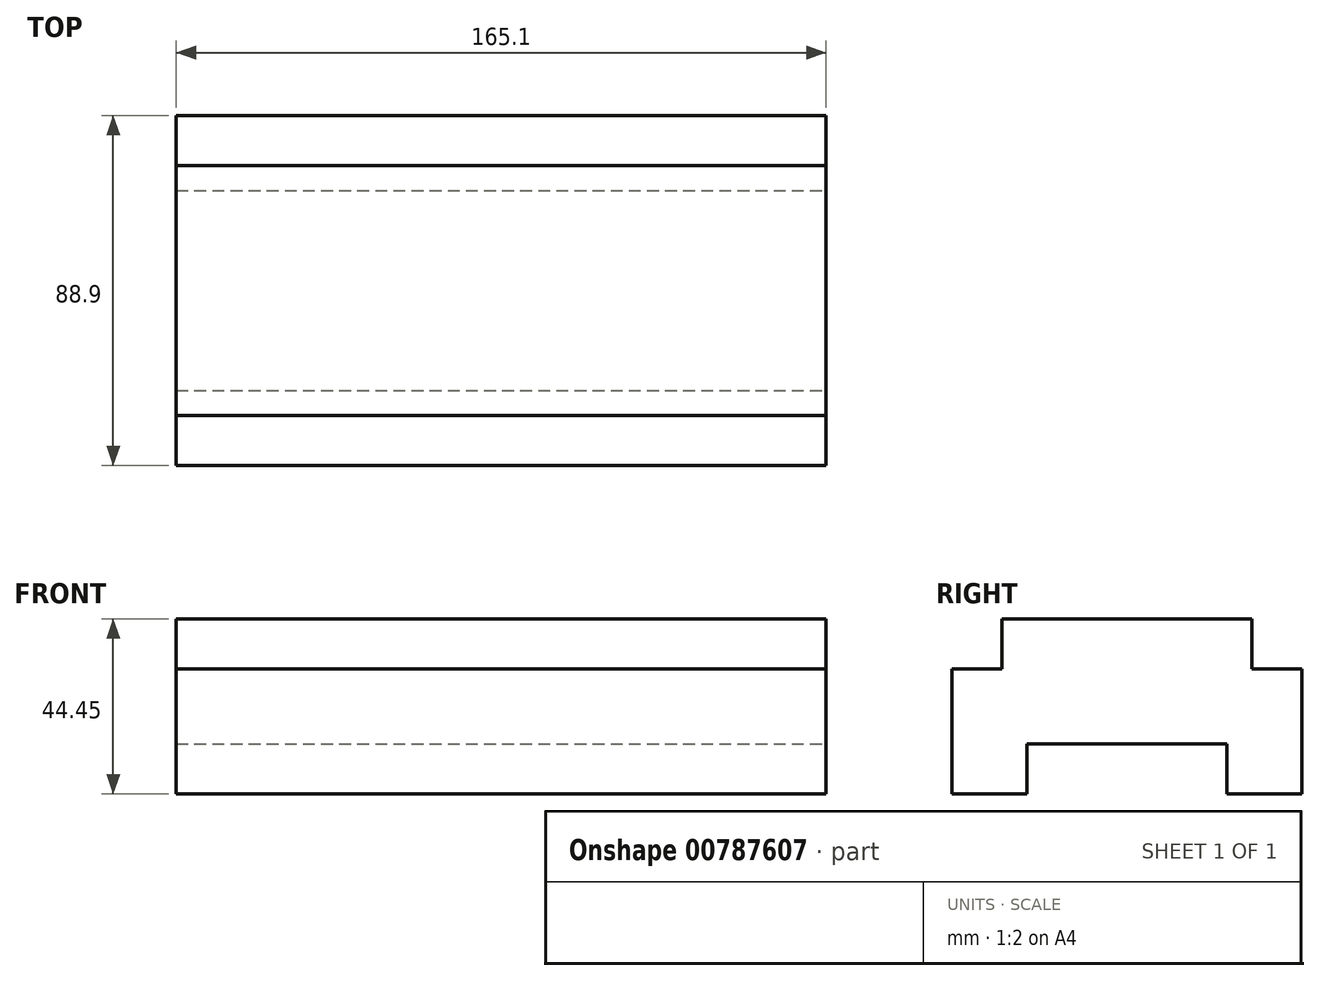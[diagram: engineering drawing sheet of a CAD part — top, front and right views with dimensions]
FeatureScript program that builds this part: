
annotation { "Feature Type Name" : "Feature", "Feature Type Description" : "" }
export const myFeature = defineFeature(function(context is Context, id is Id, definition is map)
    precondition{}
    {
        {
            var Q0;
            Q0=qCreatedBy(makeId("Front.planeOp"),FACE);
            var sketch = newSketch(context, id + "F0", { "sketchPlane" : qUnion([Q0])});
            skLineSegment(sketch, "E0", {"start": v(0, 0) * mm, "end": v(165.1, 0) * mm});
            skLineSegment(sketch, "E1", {"start": v(0, 0) * mm, "end": v(0, 44.45) * mm});
            skLineSegment(sketch, "E2", {"start": v(165.1, 0) * mm, "end": v(165.1, 44.45) * mm});
            skLineSegment(sketch, "E3", {"start": v(0, 44.45) * mm, "end": v(165.1, 44.45) * mm});
            skSolve(sketch);
        }
        {
            var Q0;
            Q0=makeQuery(id+"F0.imprint","IMPRINT",FACE,{"disambiguationData":[TD([[makeQuery(id+"F0.imprint","IMPRINT",EDGE,{"derivedFrom":sQuery(id+"F0.wireOp",EDGE,"E0")}),1.0]])]});
            extrude(context, id + "F1", {"entities" : qUnion([Q0]), "depth" : 88.9 * mm, "offsetDistance" : 25.4 * mm});
        }
        {
            var Q0;
            Q0=makeQuery(id+"F1.opExtrude","SWEPT_FACE",FACE,{"disambiguationData":[OSD([sQuery(id+"F0.wireOp",EDGE,"E2")])]});
            var sketch = newSketch(context, id + "F2", { "sketchPlane" : qUnion([Q0])});
            skLineSegment(sketch, "E4", {"start": v(-69.85, 0) * mm, "end": v(-69.85, 12.7) * mm});
            skLineSegment(sketch, "E5", {"start": v(-69.85, 12.7) * mm, "end": v(-19.05, 12.7) * mm});
            skLineSegment(sketch, "E6", {"start": v(-19.05, 12.7) * mm, "end": v(-19.05, 0) * mm});
            skSolve(sketch);
        }
        {
            var Q0;
            {var subQ0=sQuery(id+"F2.wireOp",EDGE,"E4");Q0=makeQuery(id+"F2.imprint","IMPRINT",FACE,{"disambiguationData":[TD([[makeQuery(id+"F2.imprint","IMPRINT",EDGE,{"derivedFrom":subQ0}),-1.0]])]});}
            extrude(context, id + "F3", {"entities" : qUnion([Q0]), "operationType" : NewBodyOperationType.REMOVE, "oppositeDirection" : true, "depth" : 165.1 * mm, "offsetDistance" : 25.4 * mm});
        }
        {
            var Q0;
            Q0=makeQuery(id+"F1.opExtrude","SWEPT_FACE",FACE,{"disambiguationData":[OSD([sQuery(id+"F0.wireOp",EDGE,"E2")])]});
            var sketch = newSketch(context, id + "F4", { "sketchPlane" : qUnion([Q0])});
            skLineSegment(sketch, "E7", {"start": v(-88.9, 31.75) * mm, "end": v(-76.2, 31.75) * mm});
            skLineSegment(sketch, "E8", {"start": v(-76.2, 31.75) * mm, "end": v(-76.2, 44.45) * mm});
            skLineSegment(sketch, "E9", {"start": v(0, 31.75) * mm, "end": v(-12.7, 31.75) * mm});
            skLineSegment(sketch, "E10", {"start": v(-12.7, 31.75) * mm, "end": v(-12.7, 44.45) * mm});
            skSolve(sketch);
        }
        {
            var Q0;
            {var subQ0=sQuery(id+"F4.wireOp",EDGE,"E7");Q0=makeQuery(id+"F4.imprint","IMPRINT",FACE,{"disambiguationData":[TD([[makeQuery(id+"F4.imprint","IMPRINT",EDGE,{"derivedFrom":subQ0}),1.0]])]});}
            var Q1;
            {var subQ0=sQuery(id+"F4.wireOp",EDGE,"E9");Q1=makeQuery(id+"F4.imprint","IMPRINT",FACE,{"disambiguationData":[TD([[makeQuery(id+"F4.imprint","IMPRINT",EDGE,{"derivedFrom":subQ0}),-1.0]])]});}
            extrude(context, id + "F5", {"entities" : qUnion([Q0, Q1]), "operationType" : NewBodyOperationType.REMOVE, "oppositeDirection" : true, "depth" : 165.1 * mm, "offsetDistance" : 25.4 * mm});
        }
    });
